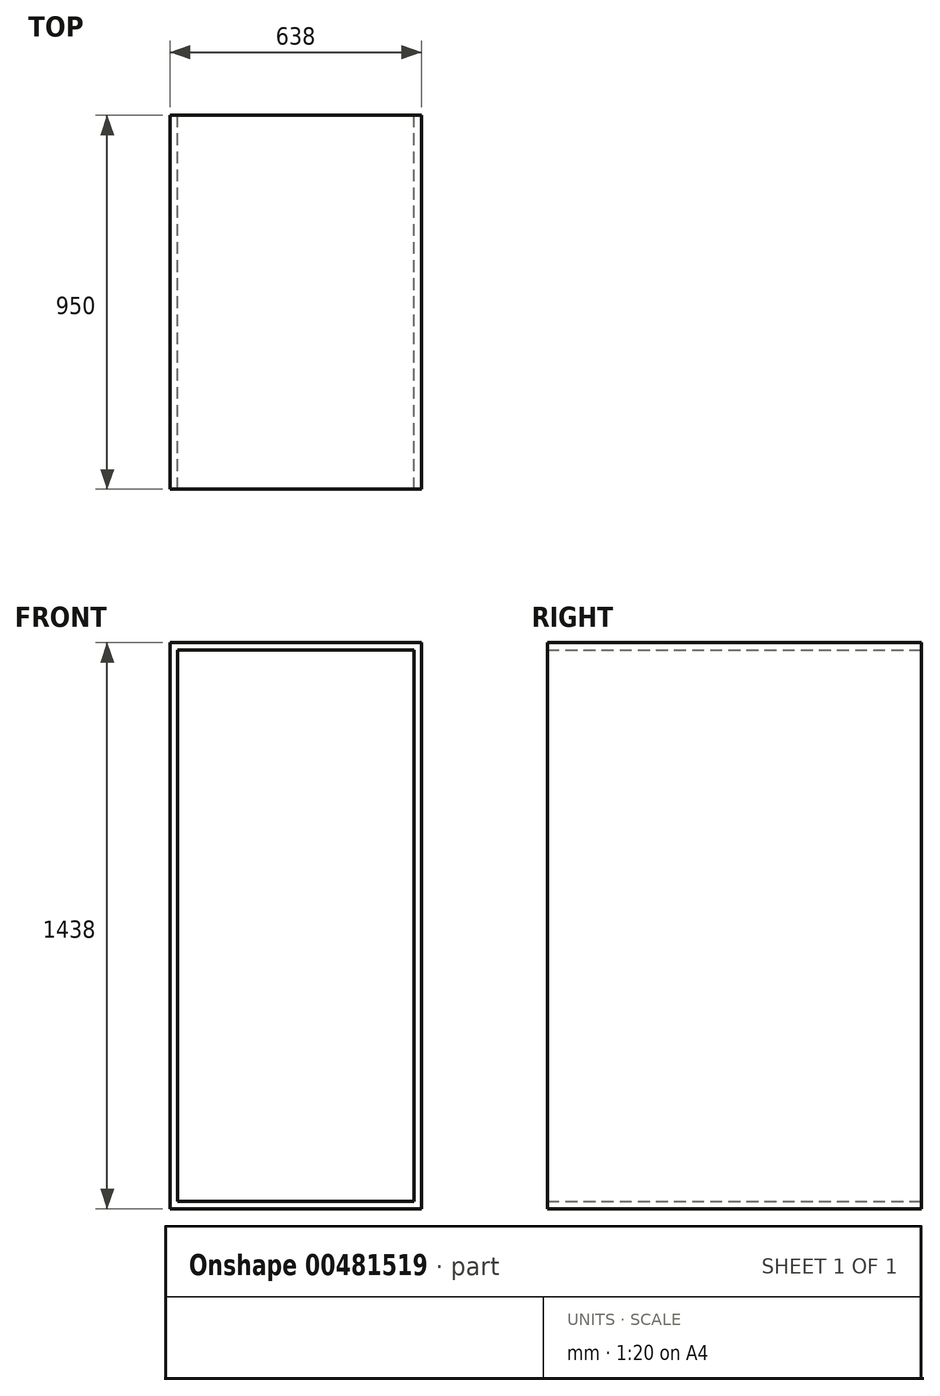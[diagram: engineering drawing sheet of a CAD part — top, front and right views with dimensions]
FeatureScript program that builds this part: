
annotation { "Feature Type Name" : "Feature", "Feature Type Description" : "" }
export const myFeature = defineFeature(function(context is Context, id is Id, definition is map)
    precondition{}
    {
        {
            var Q0;
            Q0=qCreatedBy(makeId("Front.planeOp"),FACE);
            var sketch = newSketch(context, id + "F0", { "sketchPlane" : qUnion([Q0])});
            skLineSegment(sketch, "E0.bottom", {"start": v(300, -700) * mm, "end": v(-300, -700) * mm});
            skLineSegment(sketch, "E0.top", {"start": v(300, 700) * mm, "end": v(-300, 700) * mm});
            skLineSegment(sketch, "E0.left", {"start": v(300, -700) * mm, "end": v(300, 700) * mm});
            skLineSegment(sketch, "E0.right", {"start": v(-300, -700) * mm, "end": v(-300, 700) * mm});
            skPoint(sketch, "E0.middle", {"position": v(0, 0) * mm});
            skLineSegment(sketch, "E1.bottom", {"start": v(319, -719) * mm, "end": v(-319, -719) * mm});
            skLineSegment(sketch, "E1.top", {"start": v(319, 719) * mm, "end": v(-319, 719) * mm});
            skLineSegment(sketch, "E1.left", {"start": v(319, -719) * mm, "end": v(319, 719) * mm});
            skLineSegment(sketch, "E1.right", {"start": v(-319, -719) * mm, "end": v(-319, 719) * mm});
            skSolve(sketch);
        }
        {
            var Q0;
            Q0 = qSketchRegion(id + "F0", true);
            extrude(context, id + "F1", {"entities" : qUnion([Q0]), "depth" : 950 * mm});
        }
        {
            var Q0;
            Q0=makeQuery(id+"F1.opExtrude","CAP_FACE",FACE,{"disambiguationData":[OSD([sQuery(id+"F0.wireOp",EDGE,"E0.bottom"),sQuery(id+"F0.wireOp",EDGE,"E0.top"),sQuery(id+"F0.wireOp",EDGE,"E0.left"),sQuery(id+"F0.wireOp",EDGE,"E0.right"),sQuery(id+"F0.wireOp",EDGE,"E1.bottom"),sQuery(id+"F0.wireOp",EDGE,"E1.top"),sQuery(id+"F0.wireOp",EDGE,"E1.left"),sQuery(id+"F0.wireOp",EDGE,"E1.right")])],"isStart":false});
            cPlane(context, id + "F2", {"entities" : qUnion([Q0]), "cplaneType" : CPlaneType.OFFSET, "offset" : 20 * mm, "oppositeDirection" : true, "width" : 150 * mm, "height" : 150 * mm});
        }
    });
